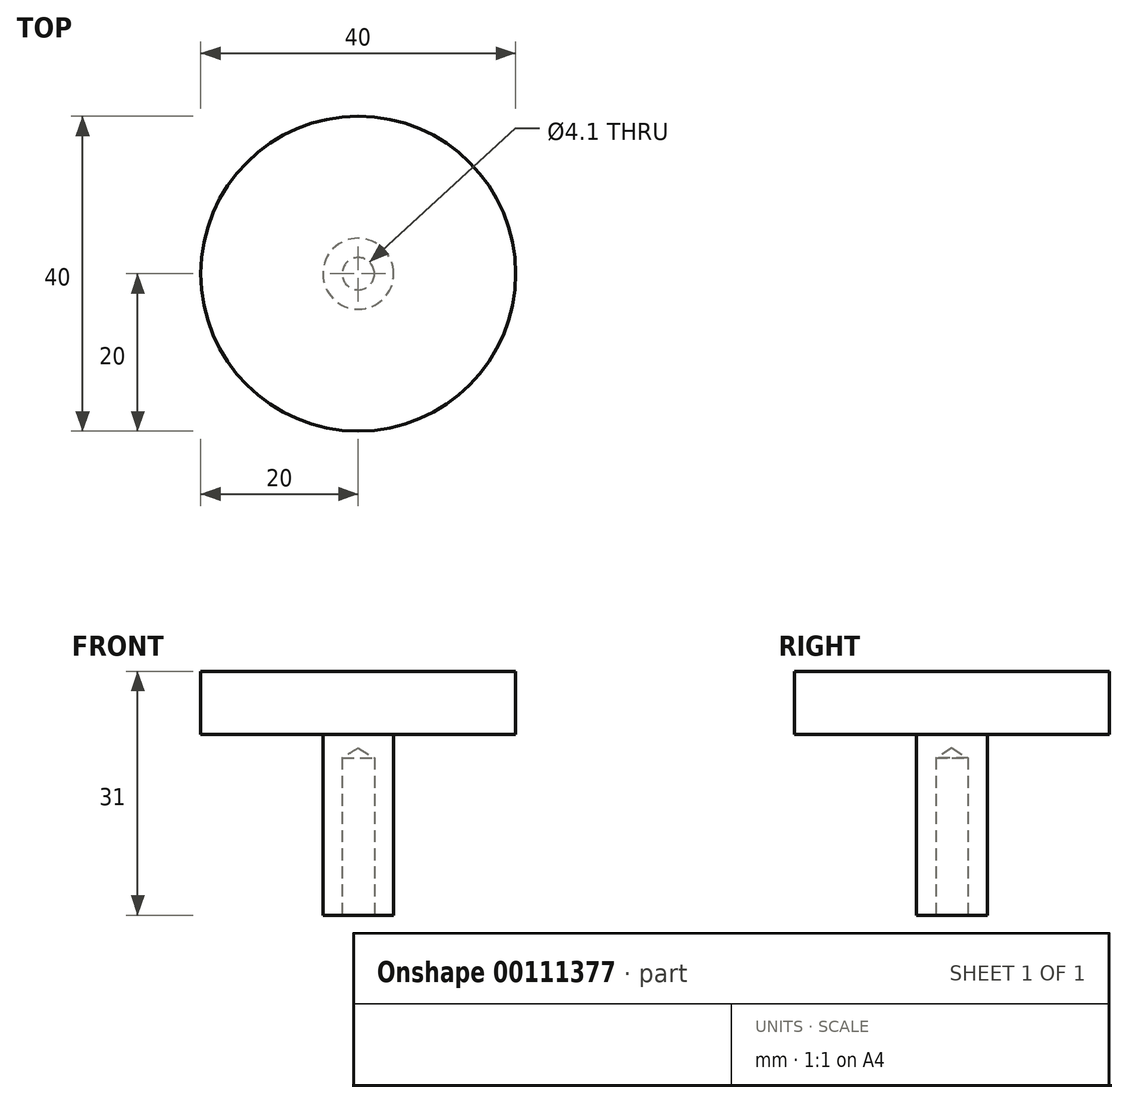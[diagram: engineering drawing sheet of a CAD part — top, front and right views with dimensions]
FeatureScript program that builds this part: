
annotation { "Feature Type Name" : "Feature", "Feature Type Description" : "" }
export const myFeature = defineFeature(function(context is Context, id is Id, definition is map)
    precondition{}
    {
        {
            var Q0;
            Q0=qCreatedBy(makeId("Top.planeOp"),FACE);
            var sketch = newSketch(context, id + "F0", { "sketchPlane" : qUnion([Q0])});
            skCircle(sketch, "E0", {"center": v(0, 0) * mm, "radius": 20 * mm});
            skSolve(sketch);
        }
        {
            var Q0;
            Q0 = qSketchRegion(id + "F0", true);
            extrude(context, id + "F1", {"entities" : qUnion([Q0]), "oppositeDirection" : true, "depth" : 8 * mm});
        }
        {
            var Q0;
            Q0=makeQuery(id+"F1.opExtrude","CAP_FACE",FACE,{"disambiguationData":[OSD([sQuery(id+"F0.wireOp",EDGE,"E0")])],"isStart":false});
            var sketch = newSketch(context, id + "F2", { "sketchPlane" : qUnion([Q0])});
            skCircle(sketch, "E1", {"center": v(0, 0) * mm, "radius": 4.5 * mm});
            skSolve(sketch);
        }
        {
            var Q0;
            Q0=makeQuery(id+"F2.imprint","IMPRINT",FACE,{"disambiguationData":[TD([[makeQuery(id+"F2.imprint","IMPRINT",EDGE,{"derivedFrom":sQuery(id+"F2.wireOp",EDGE,"E1")}),1.0]])]});
            extrude(context, id + "F3", {"entities" : qUnion([Q0]), "operationType" : NewBodyOperationType.ADD, "depth" : 23 * mm});
        }
        {
            var Q0;
            Q0=makeQuery(id+"F3.opExtrude","CAP_FACE",FACE,{"disambiguationData":[OSD([sQuery(id+"F2.wireOp",EDGE,"E1")])],"isStart":false});
            var sketch = newSketch(context, id + "F4", { "sketchPlane" : qUnion([Q0])});
            skPoint(sketch, "E2", {"position": v(0, 0) * mm});
            skSolve(sketch);
        }
        {
            var Q0;
            Q0=sQuery(id+"F4.wireOp",VERTEX,"E2");
            var Q1;
            Q1=makeQuery(id+"F1.opExtrude","SWEPT_BODY",BODY,{"disambiguationData":[OSD([sQuery(id+"F0.wireOp",EDGE,"E0")])]});
            hole(context, id + "F5", {"style" : HoleStyle.SIMPLE, "endStyle" : HoleEndStyle.BLIND, "standardTappedOrClearance" : lookupTablePath({ "standard" : "ISO", "engagement" : "75%", "pitch" : "0.9 mm", "size" : "M5", "type" : "Tapped" }), "standardBlindInLast" : lookupTablePath({ "standard" : "ISO", "engagement" : "75%", "pitch" : "0.9 mm", "size" : "M5", "type" : "Tapped" }), "holeDiameter" : 4.1 * mm, "holeDepth" : 20 * mm, "locations" : qUnion([Q0]), "scope" : qUnion([Q1])});
        }
    });
